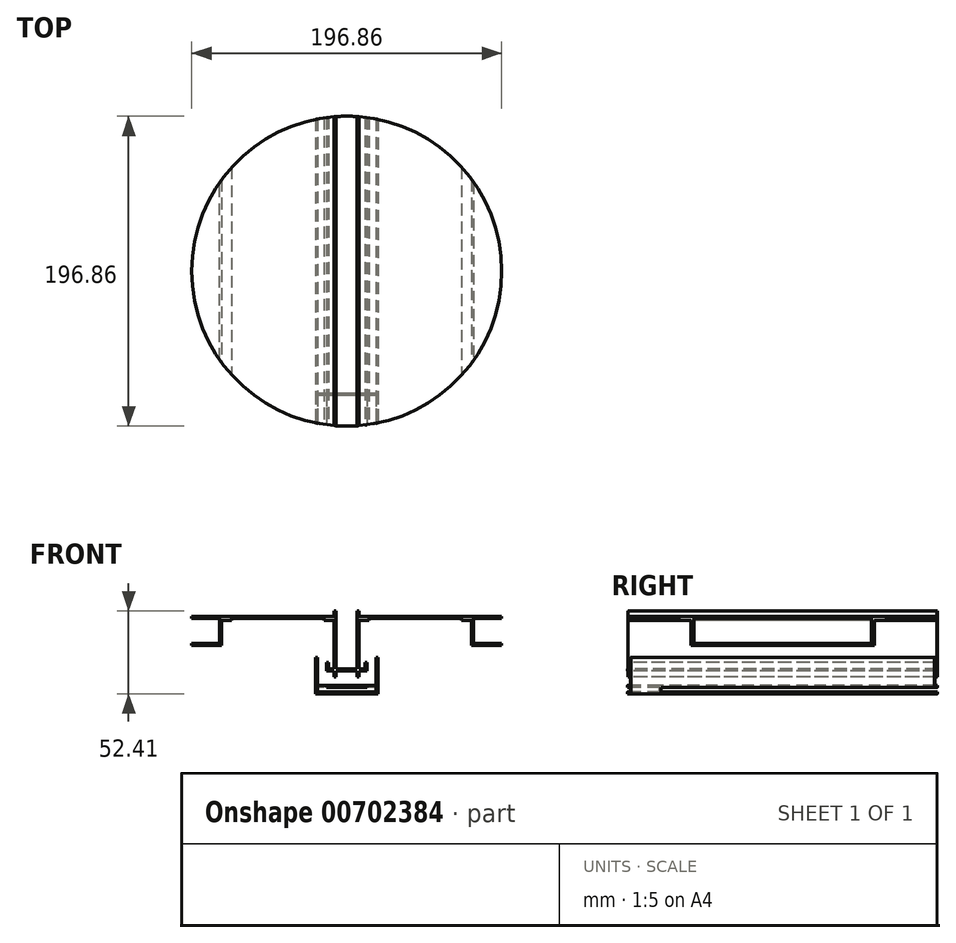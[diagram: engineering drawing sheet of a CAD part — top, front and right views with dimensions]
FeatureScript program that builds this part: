
annotation { "Feature Type Name" : "Feature", "Feature Type Description" : "" }
export const myFeature = defineFeature(function(context is Context, id is Id, definition is map)
    precondition{}
    {
        {
            var Q0;
            Q0=qCreatedBy(makeId("Top.planeOp"),FACE);
            var sketch = newSketch(context, id + "F0", { "sketchPlane" : qUnion([Q0])});
            skCircle(sketch, "E0", {"center": v(0, 0) * mm, "radius": 98.42 * mm});
            skLineSegment(sketch, "E1", {"start": v(0, 98.42) * mm, "end": v(0, -98.42) * mm, "construction": true});
            skLineSegment(sketch, "E2", {"start": v(-79.11, 58.56) * mm, "end": v(-79.11, -58.56) * mm, "construction": true});
            skLineSegment(sketch, "E3", {"start": v(79.11, 58.56) * mm, "end": v(79.11, -58.56) * mm, "construction": true});
            skLineSegment(sketch, "E4", {"start": v(0, 0) * mm, "end": v(79.11, 0) * mm, "construction": true});
            skLineSegment(sketch, "E5", {"start": v(79.11, 0) * mm, "end": v(98.42, 0) * mm, "construction": true});
            skLineSegment(sketch, "E6", {"start": v(0, 0) * mm, "end": v(-79.11, 0) * mm, "construction": true});
            skLineSegment(sketch, "E7", {"start": v(-79.11, 0) * mm, "end": v(-98.42, 0) * mm, "construction": true});
            skLineSegment(sketch, "E8", {"start": v(-7.94, 98.1) * mm, "end": v(-7.94, -98.1) * mm});
            skLineSegment(sketch, "E9", {"start": v(7.94, 98.1) * mm, "end": v(7.94, -98.1) * mm});
            skSolve(sketch);
        }
        {
            var Q0;
            {var subQ0=sQuery(id+"F0.wireOp",EDGE,"E8");Q0=makeQuery(id+"F0.imprint","IMPRINT",FACE,{"disambiguationData":[TD([[makeQuery(id+"F0.imprint","IMPRINT",EDGE,{"derivedFrom":subQ0}),-1.0]])]});}
            var Q1;
            {var subQ0=sQuery(id+"F0.wireOp",EDGE,"E9");Q1=makeQuery(id+"F0.imprint","IMPRINT",FACE,{"disambiguationData":[TD([[makeQuery(id+"F0.imprint","IMPRINT",EDGE,{"derivedFrom":subQ0}),1.0]])]});}
            extrude(context, id + "F1", {"entities" : qUnion([Q0, Q1]), "depth" : 1.27 * mm, "offsetDistance" : 25.4 * mm});
        }
        {
            var Q0;
            Q0=qCreatedBy(makeId("Top.planeOp"),FACE);
            var sketch = newSketch(context, id + "F2", { "sketchPlane" : qUnion([Q0])});
            skCircle(sketch, "E10", {"center": v(0, 0) * mm, "radius": 98.43 * mm, "construction": true});
            skLineSegment(sketch, "E11", {"start": v(0, 98.43) * mm, "end": v(0, -98.43) * mm, "construction": true});
            skLineSegment(sketch, "E12", {"start": v(-7.94, 98.1) * mm, "end": v(-7.94, -98.1) * mm});
            skLineSegment(sketch, "E13", {"start": v(7.94, 98.1) * mm, "end": v(7.94, -98.1) * mm});
            skLineSegment(sketch, "E14", {"start": v(-14.29, 97.38) * mm, "end": v(-14.29, -97.38) * mm});
            skLineSegment(sketch, "E15", {"start": v(14.29, 97.38) * mm, "end": v(14.29, -97.38) * mm});
            skLineSegment(sketch, "E16", {"start": v(-6.67, 98.2) * mm, "end": v(-6.67, -98.2) * mm});
            skLineSegment(sketch, "E17", {"start": v(6.67, -98.2) * mm, "end": v(6.67, 98.2) * mm});
            skArc(sketch, "E18", {"start": v(-14.29, 97.38) * mm, "mid": v(-11.12, 97.8) * mm, "end": v(-7.94, 98.1) * mm});
            skArc(sketch, "E19", {"start": v(-7.94, 98.1) * mm, "mid": v(-7.3, 98.15) * mm, "end": v(-6.67, 98.2) * mm});
            skArc(sketch, "E20", {"start": v(6.67, 98.2) * mm, "mid": v(7.3, 98.15) * mm, "end": v(7.94, 98.1) * mm});
            skArc(sketch, "E21", {"start": v(7.94, 98.1) * mm, "mid": v(11.12, 97.8) * mm, "end": v(14.29, 97.38) * mm});
            skArc(sketch, "E22", {"start": v(14.29, -97.38) * mm, "mid": v(11.12, -97.8) * mm, "end": v(7.94, -98.1) * mm});
            skArc(sketch, "E23", {"start": v(7.94, -98.1) * mm, "mid": v(7.3, -98.15) * mm, "end": v(6.67, -98.2) * mm});
            skArc(sketch, "E24", {"start": v(-6.67, -98.2) * mm, "mid": v(-7.3, -98.15) * mm, "end": v(-7.94, -98.1) * mm});
            skArc(sketch, "E25", {"start": v(-7.94, -98.1) * mm, "mid": v(-11.12, -97.8) * mm, "end": v(-14.29, -97.38) * mm});
            skSolve(sketch);
        }
        {
            var Q0;
            Q0=makeQuery(id+"F2.imprint","IMPRINT",FACE,{"disambiguationData":[TD([[makeQuery(id+"F2.imprint","IMPRINT",EDGE,{"derivedFrom":sQuery(id+"F2.wireOp",EDGE,"E12")}),-1.0]])]});
            var Q1;
            Q1=makeQuery(id+"F2.imprint","IMPRINT",FACE,{"disambiguationData":[TD([[makeQuery(id+"F2.imprint","IMPRINT",EDGE,{"derivedFrom":sQuery(id+"F2.wireOp",EDGE,"E13")}),1.0]])]});
            extrude(context, id + "F3", {"entities" : qUnion([Q0, Q1]), "oppositeDirection" : true, "depth" : 1.27 * mm, "offsetDistance" : 25.4 * mm});
        }
        {
            var Q0;
            Q0=makeQuery(id+"F2.imprint","IMPRINT",FACE,{"disambiguationData":[TD([[makeQuery(id+"F2.imprint","IMPRINT",EDGE,{"derivedFrom":sQuery(id+"F2.wireOp",EDGE,"E12")}),1.0]])]});
            var Q1;
            Q1=makeQuery(id+"F2.imprint","IMPRINT",FACE,{"disambiguationData":[TD([[makeQuery(id+"F2.imprint","IMPRINT",EDGE,{"derivedFrom":sQuery(id+"F2.wireOp",EDGE,"E13")}),-1.0]])]});
            extrude(context, id + "F4", {"entities" : qUnion([Q0, Q1]), "operationType" : NewBodyOperationType.ADD, "depth" : 4.5 * mm, "offsetDistance" : 25.4 * mm, "hasSecondDirection" : true, "secondDirectionOppositeDirection" : true, "secondDirectionDepth" : 29.3 * mm});
        }
        {
            var Q0;
            Q0=makeQuery(id+"F2.imprint","IMPRINT",FACE,{"disambiguationData":[TD([[makeQuery(id+"F2.imprint","IMPRINT",EDGE,{"derivedFrom":sQuery(id+"F2.wireOp",EDGE,"E12")}),-1.0]])]});
            var Q1;
            Q1=makeQuery(id+"F2.imprint","IMPRINT",FACE,{"disambiguationData":[TD([[makeQuery(id+"F2.imprint","IMPRINT",EDGE,{"derivedFrom":sQuery(id+"F2.wireOp",EDGE,"E13")}),1.0]])]});
            extrude(context, id + "F5", {"entities" : qUnion([Q0, Q1]), "oppositeDirection" : true, "depth" : 1.27 * mm, "offsetDistance" : 25.4 * mm});
        }
        {
            var Q0;
            Q0=makeQuery(id+"F2.imprint","IMPRINT",FACE,{"disambiguationData":[TD([[makeQuery(id+"F2.imprint","IMPRINT",EDGE,{"derivedFrom":sQuery(id+"F2.wireOp",EDGE,"E12")}),1.0]])]});
            var Q1;
            Q1=makeQuery(id+"F2.imprint","IMPRINT",FACE,{"disambiguationData":[TD([[makeQuery(id+"F2.imprint","IMPRINT",EDGE,{"derivedFrom":sQuery(id+"F2.wireOp",EDGE,"E13")}),-1.0]])]});
            extrude(context, id + "F6", {"entities" : qUnion([Q0, Q1]), "operationType" : NewBodyOperationType.ADD, "depth" : 3.45 * mm, "offsetDistance" : 25.4 * mm, "hasSecondDirection" : true, "secondDirectionOppositeDirection" : true, "secondDirectionDepth" : 30.63 * mm});
        }
        {
            var Q0;
            Q0=makeQuery(id+"F2.imprint","IMPRINT",FACE,{"disambiguationData":[TD([[makeQuery(id+"F2.imprint","IMPRINT",EDGE,{"derivedFrom":sQuery(id+"F2.wireOp",EDGE,"E12")}),-1.0]])]});
            var Q1;
            Q1=makeQuery(id+"F2.imprint","IMPRINT",FACE,{"disambiguationData":[TD([[makeQuery(id+"F2.imprint","IMPRINT",EDGE,{"derivedFrom":sQuery(id+"F2.wireOp",EDGE,"E13")}),1.0]])]});
            extrude(context, id + "F7", {"entities" : qUnion([Q0, Q1]), "oppositeDirection" : true, "depth" : 1.27 * mm, "offsetDistance" : 25.4 * mm});
        }
        {
            var Q0;
            Q0=makeQuery(id+"F2.imprint","IMPRINT",FACE,{"disambiguationData":[TD([[makeQuery(id+"F2.imprint","IMPRINT",EDGE,{"derivedFrom":sQuery(id+"F2.wireOp",EDGE,"E12")}),1.0]])]});
            var Q1;
            Q1=makeQuery(id+"F2.imprint","IMPRINT",FACE,{"disambiguationData":[TD([[makeQuery(id+"F2.imprint","IMPRINT",EDGE,{"derivedFrom":sQuery(id+"F2.wireOp",EDGE,"E13")}),-1.0]])]});
            extrude(context, id + "F8", {"entities" : qUnion([Q0, Q1]), "operationType" : NewBodyOperationType.ADD, "depth" : 3.45 * mm, "offsetDistance" : 25.4 * mm, "hasSecondDirection" : true, "secondDirectionOppositeDirection" : true, "secondDirectionDepth" : 36.98 * mm});
        }
        {
            var Q0;
            Q0=makeQuery(id+"F2.imprint","IMPRINT",FACE,{"disambiguationData":[TD([[makeQuery(id+"F2.imprint","IMPRINT",EDGE,{"derivedFrom":sQuery(id+"F2.wireOp",EDGE,"E12")}),-1.0]])]});
            var Q1;
            Q1=makeQuery(id+"F2.imprint","IMPRINT",FACE,{"disambiguationData":[TD([[makeQuery(id+"F2.imprint","IMPRINT",EDGE,{"derivedFrom":sQuery(id+"F2.wireOp",EDGE,"E13")}),1.0]])]});
            extrude(context, id + "F9", {"entities" : qUnion([Q0, Q1]), "oppositeDirection" : true, "depth" : 1.27 * mm, "offsetDistance" : 25.4 * mm});
        }
        {
            var Q0;
            Q0=makeQuery(id+"F2.imprint","IMPRINT",FACE,{"disambiguationData":[TD([[makeQuery(id+"F2.imprint","IMPRINT",EDGE,{"derivedFrom":sQuery(id+"F2.wireOp",EDGE,"E12")}),1.0]])]});
            var Q1;
            Q1=makeQuery(id+"F2.imprint","IMPRINT",FACE,{"disambiguationData":[TD([[makeQuery(id+"F2.imprint","IMPRINT",EDGE,{"derivedFrom":sQuery(id+"F2.wireOp",EDGE,"E13")}),-1.0]])]});
            extrude(context, id + "F10", {"entities" : qUnion([Q0, Q1]), "operationType" : NewBodyOperationType.ADD, "depth" : 3.45 * mm, "offsetDistance" : 25.4 * mm, "hasSecondDirection" : true, "secondDirectionOppositeDirection" : true, "secondDirectionDepth" : 37.24 * mm});
        }
        {
            var Q0;
            Q0=makeQuery(id+"F2.imprint","IMPRINT",FACE,{"disambiguationData":[TD([[makeQuery(id+"F2.imprint","IMPRINT",EDGE,{"derivedFrom":sQuery(id+"F2.wireOp",EDGE,"E12")}),-1.0]])]});
            var Q1;
            Q1=makeQuery(id+"F2.imprint","IMPRINT",FACE,{"disambiguationData":[TD([[makeQuery(id+"F2.imprint","IMPRINT",EDGE,{"derivedFrom":sQuery(id+"F2.wireOp",EDGE,"E13")}),1.0]])]});
            extrude(context, id + "F11", {"entities" : qUnion([Q0, Q1]), "oppositeDirection" : true, "depth" : 1.27 * mm, "offsetDistance" : 25.4 * mm});
        }
        {
            var Q0;
            Q0=makeQuery(id+"F2.imprint","IMPRINT",FACE,{"disambiguationData":[TD([[makeQuery(id+"F2.imprint","IMPRINT",EDGE,{"derivedFrom":sQuery(id+"F2.wireOp",EDGE,"E12")}),1.0]])]});
            var Q1;
            Q1=makeQuery(id+"F2.imprint","IMPRINT",FACE,{"disambiguationData":[TD([[makeQuery(id+"F2.imprint","IMPRINT",EDGE,{"derivedFrom":sQuery(id+"F2.wireOp",EDGE,"E13")}),-1.0]])]});
            extrude(context, id + "F12", {"entities" : qUnion([Q0, Q1]), "operationType" : NewBodyOperationType.ADD, "depth" : 3.45 * mm, "offsetDistance" : 25.4 * mm, "hasSecondDirection" : true, "secondDirectionOppositeDirection" : true, "secondDirectionDepth" : 30.9 * mm});
        }
        {
            var Q0;
            Q0=qCreatedBy(makeId("Top.planeOp"),FACE);
            var sketch = newSketch(context, id + "F13", { "sketchPlane" : qUnion([Q0])});
            skCircle(sketch, "E26", {"center": v(0, 0) * mm, "radius": 98.43 * mm, "construction": true});
            skLineSegment(sketch, "E27", {"start": v(-98.43, 0) * mm, "end": v(98.43, 0) * mm, "construction": true});
            skLineSegment(sketch, "E28", {"start": v(0, 98.43) * mm, "end": v(0, -98.43) * mm, "construction": true});
            skLineSegment(sketch, "E29", {"start": v(-7.94, 98.1) * mm, "end": v(-7.94, -98.1) * mm});
            skLineSegment(sketch, "E30", {"start": v(7.94, 98.1) * mm, "end": v(7.94, -98.1) * mm});
            skLineSegment(sketch, "E31", {"start": v(79.38, 58.2) * mm, "end": v(79.38, -58.2) * mm});
            skLineSegment(sketch, "E32", {"start": v(-79.38, 58.2) * mm, "end": v(-79.38, -58.2) * mm});
            skLineSegment(sketch, "E33", {"start": v(-14.29, 97.38) * mm, "end": v(-14.29, -97.38) * mm});
            skLineSegment(sketch, "E34", {"start": v(14.29, 97.38) * mm, "end": v(14.29, -97.38) * mm});
            skLineSegment(sketch, "E35", {"start": v(-6.67, 98.2) * mm, "end": v(-6.67, -98.2) * mm});
            skLineSegment(sketch, "E36", {"start": v(6.67, 98.2) * mm, "end": v(6.67, -98.2) * mm});
            skLineSegment(sketch, "E37", {"start": v(-73.03, 66) * mm, "end": v(-73.03, -66) * mm});
            skLineSegment(sketch, "E38", {"start": v(-80.65, 56.43) * mm, "end": v(-80.65, -56.43) * mm});
            skLineSegment(sketch, "E39", {"start": v(73.03, 66) * mm, "end": v(73.03, -66) * mm});
            skLineSegment(sketch, "E40", {"start": v(80.65, 56.43) * mm, "end": v(80.65, -56.43) * mm});
            skArc(sketch, "E41", {"start": v(-6.67, -98.2) * mm, "mid": v(-98.43, 0) * mm, "end": v(-6.67, 98.2) * mm});
            skArc(sketch, "E42", {"start": v(6.67, -98.2) * mm, "mid": v(98.43, 0) * mm, "end": v(6.67, 98.2) * mm});
            skSolve(sketch);
        }
        {
            var Q0;
            {var subQ0=sQuery(id+"F13.wireOp",EDGE,"E32");Q0=makeQuery(id+"F13.imprint","IMPRINT",FACE,{"disambiguationData":[TD([[makeQuery(id+"F13.imprint","IMPRINT",EDGE,{"derivedFrom":subQ0}),1.0]])]});}
            var Q1;
            {var subQ0=sQuery(id+"F13.wireOp",EDGE,"E33");Q1=makeQuery(id+"F13.imprint","IMPRINT",FACE,{"disambiguationData":[TD([[makeQuery(id+"F13.imprint","IMPRINT",EDGE,{"derivedFrom":subQ0}),-1.0]])]});}
            var Q2;
            {var subQ0=sQuery(id+"F13.wireOp",EDGE,"E29");Q2=makeQuery(id+"F13.imprint","IMPRINT",FACE,{"disambiguationData":[TD([[makeQuery(id+"F13.imprint","IMPRINT",EDGE,{"derivedFrom":subQ0}),-1.0]])]});}
            var Q3;
            {var subQ0=sQuery(id+"F13.wireOp",EDGE,"E30");Q3=makeQuery(id+"F13.imprint","IMPRINT",FACE,{"disambiguationData":[TD([[makeQuery(id+"F13.imprint","IMPRINT",EDGE,{"derivedFrom":subQ0}),1.0]])]});}
            var Q4;
            {var subQ0=sQuery(id+"F13.wireOp",EDGE,"E34");Q4=makeQuery(id+"F13.imprint","IMPRINT",FACE,{"disambiguationData":[TD([[makeQuery(id+"F13.imprint","IMPRINT",EDGE,{"derivedFrom":subQ0}),1.0]])]});}
            var Q5;
            {var subQ0=sQuery(id+"F13.wireOp",EDGE,"E31");Q5=makeQuery(id+"F13.imprint","IMPRINT",FACE,{"disambiguationData":[TD([[makeQuery(id+"F13.imprint","IMPRINT",EDGE,{"derivedFrom":subQ0}),-1.0]])]});}
            extrude(context, id + "F14", {"entities" : qUnion([Q0, Q1, Q2, Q3, Q4, Q5]), "depth" : 1.27 * mm, "offsetDistance" : 25.4 * mm});
        }
        {
            var Q0;
            {var subQ0=sQuery(id+"F13.wireOp",EDGE,"E29");Q0=makeQuery(id+"F13.imprint","IMPRINT",FACE,{"disambiguationData":[TD([[makeQuery(id+"F13.imprint","IMPRINT",EDGE,{"derivedFrom":subQ0}),-1.0]])]});}
            var Q1;
            {var subQ0=sQuery(id+"F13.wireOp",EDGE,"E30");Q1=makeQuery(id+"F13.imprint","IMPRINT",FACE,{"disambiguationData":[TD([[makeQuery(id+"F13.imprint","IMPRINT",EDGE,{"derivedFrom":subQ0}),1.0]])]});}
            extrude(context, id + "F15", {"entities" : qUnion([Q0, Q1]), "oppositeDirection" : true, "depth" : 1.27 * mm, "offsetDistance" : 25.4 * mm});
        }
        {
            var Q0;
            {var subQ0=sQuery(id+"F13.wireOp",EDGE,"E29");Q0=makeQuery(id+"F13.imprint","IMPRINT",FACE,{"disambiguationData":[TD([[makeQuery(id+"F13.imprint","IMPRINT",EDGE,{"derivedFrom":subQ0}),1.0]])]});}
            var Q1;
            {var subQ0=sQuery(id+"F13.wireOp",EDGE,"E30");Q1=makeQuery(id+"F13.imprint","IMPRINT",FACE,{"disambiguationData":[TD([[makeQuery(id+"F13.imprint","IMPRINT",EDGE,{"derivedFrom":subQ0}),-1.0]])]});}
            extrude(context, id + "F16", {"entities" : qUnion([Q0, Q1]), "operationType" : NewBodyOperationType.ADD, "depth" : 3.45 * mm, "offsetDistance" : 25.4 * mm, "hasSecondDirection" : true, "secondDirectionOppositeDirection" : true, "secondDirectionDepth" : 30.63 * mm});
        }
        {
            var Q0;
            {var subQ0=sQuery(id+"F13.wireOp",EDGE,"E32");Q0=makeQuery(id+"F13.imprint","IMPRINT",FACE,{"disambiguationData":[TD([[makeQuery(id+"F13.imprint","IMPRINT",EDGE,{"derivedFrom":subQ0}),1.0]])]});}
            var Q1;
            {var subQ0=sQuery(id+"F13.wireOp",EDGE,"E31");Q1=makeQuery(id+"F13.imprint","IMPRINT",FACE,{"disambiguationData":[TD([[makeQuery(id+"F13.imprint","IMPRINT",EDGE,{"derivedFrom":subQ0}),-1.0]])]});}
            extrude(context, id + "F17", {"entities" : qUnion([Q0, Q1]), "oppositeDirection" : true, "depth" : 1.27 * mm, "offsetDistance" : 25.4 * mm});
        }
        {
            var Q0;
            {var subQ0=sQuery(id+"F13.wireOp",EDGE,"E32");Q0=makeQuery(id+"F13.imprint","IMPRINT",FACE,{"disambiguationData":[TD([[makeQuery(id+"F13.imprint","IMPRINT",EDGE,{"derivedFrom":subQ0}),-1.0]])]});}
            var Q1;
            {var subQ0=sQuery(id+"F13.wireOp",EDGE,"E31");Q1=makeQuery(id+"F13.imprint","IMPRINT",FACE,{"disambiguationData":[TD([[makeQuery(id+"F13.imprint","IMPRINT",EDGE,{"derivedFrom":subQ0}),1.0]])]});}
            extrude(context, id + "F18", {"entities" : qUnion([Q0, Q1]), "operationType" : NewBodyOperationType.ADD, "depth" : 1.27 * mm, "offsetDistance" : 25.4 * mm, "hasSecondDirection" : true, "secondDirectionOppositeDirection" : true, "secondDirectionDepth" : 15.88 * mm});
        }
        {
            var Q0;
            {var subQ0=sQuery(id+"F13.wireOp",EDGE,"E38");Q0=makeQuery(id+"F13.imprint","IMPRINT",FACE,{"disambiguationData":[TD([[makeQuery(id+"F13.imprint","IMPRINT",EDGE,{"derivedFrom":subQ0}),-1.0]])]});}
            var Q1;
            {var subQ0=sQuery(id+"F13.wireOp",EDGE,"E32");Q1=makeQuery(id+"F13.imprint","IMPRINT",FACE,{"disambiguationData":[TD([[makeQuery(id+"F13.imprint","IMPRINT",EDGE,{"derivedFrom":subQ0}),-1.0]])]});}
            var Q2;
            {var subQ0=sQuery(id+"F13.wireOp",EDGE,"E40");Q2=makeQuery(id+"F13.imprint","IMPRINT",FACE,{"disambiguationData":[TD([[makeQuery(id+"F13.imprint","IMPRINT",EDGE,{"derivedFrom":subQ0}),1.0]])]});}
            var Q3;
            {var subQ0=sQuery(id+"F13.wireOp",EDGE,"E31");Q3=makeQuery(id+"F13.imprint","IMPRINT",FACE,{"disambiguationData":[TD([[makeQuery(id+"F13.imprint","IMPRINT",EDGE,{"derivedFrom":subQ0}),1.0]])]});}
            extrude(context, id + "F19", {"entities" : qUnion([Q0, Q1, Q2, Q3]), "oppositeDirection" : true, "depth" : 17.14 * mm, "offsetDistance" : 25.4 * mm, "hasSecondDirection" : true, "secondDirectionOppositeDirection" : true, "secondDirectionDepth" : 15.88 * mm});
        }
        {
            var Q0;
            Q0=qCreatedBy(makeId("Top.planeOp"),FACE);
            var sketch = newSketch(context, id + "F20", { "sketchPlane" : qUnion([Q0])});
            skCircle(sketch, "E43", {"center": v(0, 0) * mm, "radius": 98.43 * mm, "construction": true});
            skLineSegment(sketch, "E44", {"start": v(-98.43, 0) * mm, "end": v(98.43, 0) * mm, "construction": true});
            skLineSegment(sketch, "E45", {"start": v(0, 98.43) * mm, "end": v(0, -98.43) * mm, "construction": true});
            skLineSegment(sketch, "E46", {"start": v(-7.94, 98.1) * mm, "end": v(-7.94, -98.1) * mm});
            skLineSegment(sketch, "E47", {"start": v(7.94, 98.1) * mm, "end": v(7.94, -98.1) * mm});
            skLineSegment(sketch, "E48", {"start": v(-14.29, 97.38) * mm, "end": v(-14.29, -97.38) * mm});
            skLineSegment(sketch, "E49", {"start": v(14.29, 97.38) * mm, "end": v(14.29, -97.38) * mm});
            skLineSegment(sketch, "E50", {"start": v(-6.67, 98.2) * mm, "end": v(-6.67, -98.2) * mm});
            skLineSegment(sketch, "E51", {"start": v(6.67, 98.2) * mm, "end": v(6.67, -98.2) * mm});
            skArc(sketch, "E52", {"start": v(-14.29, 97.38) * mm, "mid": v(-10.49, 97.86) * mm, "end": v(-6.67, 98.2) * mm});
            skArc(sketch, "E53", {"start": v(6.67, 98.2) * mm, "mid": v(10.49, 97.86) * mm, "end": v(14.29, 97.38) * mm});
            skArc(sketch, "E54", {"start": v(14.29, -97.38) * mm, "mid": v(10.49, -97.86) * mm, "end": v(6.67, -98.2) * mm});
            skArc(sketch, "E55", {"start": v(-6.67, -98.2) * mm, "mid": v(-10.49, -97.86) * mm, "end": v(-14.29, -97.38) * mm});
            skSolve(sketch);
        }
        {
            var Q0;
            {var subQ0=sQuery(id+"F20.wireOp",EDGE,"E46");Q0=makeQuery(id+"F20.imprint","IMPRINT",FACE,{"disambiguationData":[TD([[makeQuery(id+"F20.imprint","IMPRINT",EDGE,{"derivedFrom":subQ0}),-1.0]])]});}
            var Q1;
            {var subQ0=sQuery(id+"F20.wireOp",EDGE,"E47");Q1=makeQuery(id+"F20.imprint","IMPRINT",FACE,{"disambiguationData":[TD([[makeQuery(id+"F20.imprint","IMPRINT",EDGE,{"derivedFrom":subQ0}),1.0]])]});}
            extrude(context, id + "F21", {"entities" : qUnion([Q0, Q1]), "oppositeDirection" : true, "depth" : 1.27 * mm, "offsetDistance" : 25.4 * mm});
        }
        {
            var Q0;
            {var subQ0=sQuery(id+"F20.wireOp",EDGE,"E46");Q0=makeQuery(id+"F20.imprint","IMPRINT",FACE,{"disambiguationData":[TD([[makeQuery(id+"F20.imprint","IMPRINT",EDGE,{"derivedFrom":subQ0}),1.0]])]});}
            var Q1;
            {var subQ0=sQuery(id+"F20.wireOp",EDGE,"E47");Q1=makeQuery(id+"F20.imprint","IMPRINT",FACE,{"disambiguationData":[TD([[makeQuery(id+"F20.imprint","IMPRINT",EDGE,{"derivedFrom":subQ0}),-1.0]])]});}
            extrude(context, id + "F22", {"entities" : qUnion([Q0, Q1]), "operationType" : NewBodyOperationType.ADD, "depth" : 3.45 * mm, "offsetDistance" : 25.4 * mm, "hasSecondDirection" : true, "secondDirectionOppositeDirection" : true, "secondDirectionDepth" : 30.16 * mm});
        }
        {
            var Q0;
            Q0=qCreatedBy(makeId("Top.planeOp"),FACE);
            var sketch = newSketch(context, id + "F23", { "sketchPlane" : qUnion([Q0])});
            skCircle(sketch, "E56", {"center": v(0, 0) * mm, "radius": 98.43 * mm, "construction": true});
            skLineSegment(sketch, "E57", {"start": v(-98.43, 0) * mm, "end": v(98.43, 0) * mm, "construction": true});
            skLineSegment(sketch, "E58", {"start": v(0, 98.43) * mm, "end": v(0, -98.43) * mm, "construction": true});
            skLineSegment(sketch, "E59", {"start": v(-11.64, 97.73) * mm, "end": v(-11.64, -97.73) * mm});
            skLineSegment(sketch, "E60", {"start": v(11.64, 97.73) * mm, "end": v(11.64, -97.73) * mm});
            skLineSegment(sketch, "E61", {"start": v(-12.91, 97.57) * mm, "end": v(-12.91, -97.57) * mm});
            skLineSegment(sketch, "E62", {"start": v(12.91, 97.57) * mm, "end": v(12.91, -97.57) * mm});
            skArc(sketch, "E63", {"start": v(-12.91, 97.57) * mm, "mid": v(0, 98.43) * mm, "end": v(12.91, 97.57) * mm});
            skArc(sketch, "E64", {"start": v(12.91, -97.57) * mm, "mid": v(0, -98.43) * mm, "end": v(-12.91, -97.57) * mm});
            skLineSegment(sketch, "E65", {"start": v(-18.65, 96.64) * mm, "end": v(-18.65, -96.64) * mm});
            skLineSegment(sketch, "E66", {"start": v(18.65, 96.64) * mm, "end": v(18.65, -96.64) * mm});
            skLineSegment(sketch, "E67", {"start": v(-19.92, 96.39) * mm, "end": v(-19.92, -96.39) * mm});
            skLineSegment(sketch, "E68", {"start": v(19.92, 96.39) * mm, "end": v(19.92, -96.39) * mm});
            skArc(sketch, "E69", {"start": v(19.92, -96.39) * mm, "mid": v(0, -98.43) * mm, "end": v(-19.92, -96.39) * mm});
            skArc(sketch, "E70", {"start": v(-19.92, 96.39) * mm, "mid": v(0, 98.43) * mm, "end": v(19.92, 96.39) * mm});
            skLineSegment(sketch, "E71", {"start": v(-19.92, -78.52) * mm, "end": v(19.92, -78.52) * mm});
            skLineSegment(sketch, "E72", {"start": v(-19.92, -77.25) * mm, "end": v(19.92, -77.25) * mm});
            skSolve(sketch);
        }
        {
            var Q0;
            {var subQ0=sQuery(id+"F23.wireOp",EDGE,"E59");Q0=makeQuery(id+"F23.imprint","IMPRINT",FACE,{"disambiguationData":[TD([[makeQuery(id+"F23.imprint","IMPRINT",EDGE,{"derivedFrom":subQ0}),-1.0]])]});}
            var Q1;
            {var subQ0=sQuery(id+"F23.wireOp",EDGE,"E60");Q1=makeQuery(id+"F23.imprint","IMPRINT",FACE,{"disambiguationData":[TD([[makeQuery(id+"F23.imprint","IMPRINT",EDGE,{"derivedFrom":subQ0}),1.0]])]});}
            extrude(context, id + "F24", {"entities" : qUnion([Q0, Q1]), "oppositeDirection" : true, "depth" : 32.08 * mm, "offsetDistance" : 25.4 * mm, "hasSecondDirection" : true, "secondDirectionOppositeDirection" : true, "secondDirectionDepth" : 28.05 * mm});
        }
        {
            var Q0;
            {var subQ0=sQuery(id+"F23.wireOp",EDGE,"E59");Q0=makeQuery(id+"F23.imprint","IMPRINT",FACE,{"disambiguationData":[TD([[makeQuery(id+"F23.imprint","IMPRINT",EDGE,{"derivedFrom":subQ0}),1.0]])]});}
            var Q1;
            {var subQ0=sQuery(id+"F23.wireOp",EDGE,"E59");Q1=makeQuery(id+"F23.imprint","IMPRINT",FACE,{"disambiguationData":[TD([[makeQuery(id+"F23.imprint","IMPRINT",EDGE,{"derivedFrom":subQ0}),-1.0]])]});}
            var Q2;
            {var subQ0=sQuery(id+"F23.wireOp",EDGE,"E60");Q2=makeQuery(id+"F23.imprint","IMPRINT",FACE,{"disambiguationData":[TD([[makeQuery(id+"F23.imprint","IMPRINT",EDGE,{"derivedFrom":subQ0}),1.0]])]});}
            extrude(context, id + "F25", {"entities" : qUnion([Q0, Q1, Q2]), "operationType" : NewBodyOperationType.ADD, "oppositeDirection" : true, "depth" : 33.35 * mm, "offsetDistance" : 25.4 * mm, "hasSecondDirection" : true, "secondDirectionOppositeDirection" : true, "secondDirectionDepth" : 32.08 * mm});
        }
        {
            var Q0;
            {var subQ0=sQuery(id+"F23.wireOp",EDGE,"E70");var subQ1=sQuery(id+"F23.wireOp",EDGE,"E66");var subQ2=makeQuery(id+"F23.imprint","INTERSECT",VERTEX,{"derivedFrom":[subQ1,subQ0]});Q0=makeQuery(id+"F23.imprint","IMPRINT",FACE,{"disambiguationData":[TD([[makeQuery(id+"F23.imprint","IMPRINT",EDGE,{"disambiguationData":[TD([[subQ2,-1.0]])],"derivedFrom":subQ1}),1.0]])]});}
            var Q1;
            {var subQ0=sQuery(id+"F23.wireOp",EDGE,"E70");var subQ1=sQuery(id+"F23.wireOp",EDGE,"E65");var subQ2=makeQuery(id+"F23.imprint","INTERSECT",VERTEX,{"derivedFrom":[subQ1,subQ0]});Q1=makeQuery(id+"F23.imprint","IMPRINT",FACE,{"disambiguationData":[TD([[makeQuery(id+"F23.imprint","IMPRINT",EDGE,{"disambiguationData":[TD([[subQ2,-1.0]])],"derivedFrom":subQ1}),-1.0]])]});}
            extrude(context, id + "F26", {"entities" : qUnion([Q0, Q1]), "oppositeDirection" : true, "depth" : 42.53 * mm, "offsetDistance" : 25.4 * mm, "hasSecondDirection" : true, "secondDirectionOppositeDirection" : true, "secondDirectionDepth" : 24.94 * mm});
        }
        {
            var Q0;
            {var subQ0=sQuery(id+"F23.wireOp",EDGE,"E70");var subQ1=sQuery(id+"F23.wireOp",EDGE,"E59");var subQ2=makeQuery(id+"F23.imprint","INTERSECT",VERTEX,{"derivedFrom":[subQ1,subQ0]});Q0=makeQuery(id+"F23.imprint","IMPRINT",FACE,{"disambiguationData":[TD([[makeQuery(id+"F23.imprint","IMPRINT",EDGE,{"disambiguationData":[TD([[subQ2,-1.0]])],"derivedFrom":subQ1}),1.0]])]});}
            var Q1;
            {var subQ0=sQuery(id+"F23.wireOp",EDGE,"E72");var subQ1=sQuery(id+"F23.wireOp",EDGE,"E59");var subQ2=makeQuery(id+"F23.imprint","INTERSECT",VERTEX,{"derivedFrom":[subQ1,subQ0]});Q1=makeQuery(id+"F23.imprint","IMPRINT",FACE,{"disambiguationData":[TD([[makeQuery(id+"F23.imprint","IMPRINT",EDGE,{"disambiguationData":[TD([[subQ2,-1.0]])],"derivedFrom":subQ1}),1.0]])]});}
            var Q2;
            {var subQ0=sQuery(id+"F23.wireOp",EDGE,"E70");var subQ1=sQuery(id+"F23.wireOp",EDGE,"E65");var subQ2=makeQuery(id+"F23.imprint","INTERSECT",VERTEX,{"derivedFrom":[subQ1,subQ0]});Q2=makeQuery(id+"F23.imprint","IMPRINT",FACE,{"disambiguationData":[TD([[makeQuery(id+"F23.imprint","IMPRINT",EDGE,{"disambiguationData":[TD([[subQ2,-1.0]])],"derivedFrom":subQ1}),-1.0]])]});}
            var Q3;
            {var subQ0=sQuery(id+"F23.wireOp",EDGE,"E72");var subQ1=sQuery(id+"F23.wireOp",EDGE,"E65");var subQ2=makeQuery(id+"F23.imprint","INTERSECT",VERTEX,{"derivedFrom":[subQ1,subQ0]});Q3=makeQuery(id+"F23.imprint","IMPRINT",FACE,{"disambiguationData":[TD([[makeQuery(id+"F23.imprint","IMPRINT",EDGE,{"disambiguationData":[TD([[subQ2,-1.0]])],"derivedFrom":subQ1}),-1.0]])]});}
            var Q4;
            {var subQ0=sQuery(id+"F23.wireOp",EDGE,"E70");var subQ1=sQuery(id+"F23.wireOp",EDGE,"E61");var subQ2=makeQuery(id+"F23.imprint","INTERSECT",VERTEX,{"derivedFrom":[subQ1,subQ0]});Q4=makeQuery(id+"F23.imprint","IMPRINT",FACE,{"disambiguationData":[TD([[makeQuery(id+"F23.imprint","IMPRINT",EDGE,{"disambiguationData":[TD([[subQ2,-1.0]])],"derivedFrom":subQ1}),-1.0]])]});}
            var Q5;
            {var subQ0=sQuery(id+"F23.wireOp",EDGE,"E72");var subQ1=sQuery(id+"F23.wireOp",EDGE,"E61");var subQ2=makeQuery(id+"F23.imprint","INTERSECT",VERTEX,{"derivedFrom":[subQ1,subQ0]});Q5=makeQuery(id+"F23.imprint","IMPRINT",FACE,{"disambiguationData":[TD([[makeQuery(id+"F23.imprint","IMPRINT",EDGE,{"disambiguationData":[TD([[subQ2,-1.0]])],"derivedFrom":subQ1}),-1.0]])]});}
            var Q6;
            {var subQ0=sQuery(id+"F23.wireOp",EDGE,"E70");var subQ1=sQuery(id+"F23.wireOp",EDGE,"E59");var subQ2=makeQuery(id+"F23.imprint","INTERSECT",VERTEX,{"derivedFrom":[subQ1,subQ0]});Q6=makeQuery(id+"F23.imprint","IMPRINT",FACE,{"disambiguationData":[TD([[makeQuery(id+"F23.imprint","IMPRINT",EDGE,{"disambiguationData":[TD([[subQ2,-1.0]])],"derivedFrom":subQ1}),-1.0]])]});}
            var Q7;
            {var subQ0=sQuery(id+"F23.wireOp",EDGE,"E72");var subQ1=sQuery(id+"F23.wireOp",EDGE,"E59");var subQ2=makeQuery(id+"F23.imprint","INTERSECT",VERTEX,{"derivedFrom":[subQ1,subQ0]});Q7=makeQuery(id+"F23.imprint","IMPRINT",FACE,{"disambiguationData":[TD([[makeQuery(id+"F23.imprint","IMPRINT",EDGE,{"disambiguationData":[TD([[subQ2,-1.0]])],"derivedFrom":subQ1}),-1.0]])]});}
            var Q8;
            {var subQ0=sQuery(id+"F23.wireOp",EDGE,"E70");var subQ1=sQuery(id+"F23.wireOp",EDGE,"E60");var subQ2=makeQuery(id+"F23.imprint","INTERSECT",VERTEX,{"derivedFrom":[subQ1,subQ0]});Q8=makeQuery(id+"F23.imprint","IMPRINT",FACE,{"disambiguationData":[TD([[makeQuery(id+"F23.imprint","IMPRINT",EDGE,{"disambiguationData":[TD([[subQ2,-1.0]])],"derivedFrom":subQ1}),1.0]])]});}
            var Q9;
            {var subQ0=sQuery(id+"F23.wireOp",EDGE,"E72");var subQ1=sQuery(id+"F23.wireOp",EDGE,"E60");var subQ2=makeQuery(id+"F23.imprint","INTERSECT",VERTEX,{"derivedFrom":[subQ1,subQ0]});Q9=makeQuery(id+"F23.imprint","IMPRINT",FACE,{"disambiguationData":[TD([[makeQuery(id+"F23.imprint","IMPRINT",EDGE,{"disambiguationData":[TD([[subQ2,-1.0]])],"derivedFrom":subQ1}),1.0]])]});}
            var Q10;
            {var subQ0=sQuery(id+"F23.wireOp",EDGE,"E70");var subQ1=sQuery(id+"F23.wireOp",EDGE,"E62");var subQ2=makeQuery(id+"F23.imprint","INTERSECT",VERTEX,{"derivedFrom":[subQ1,subQ0]});Q10=makeQuery(id+"F23.imprint","IMPRINT",FACE,{"disambiguationData":[TD([[makeQuery(id+"F23.imprint","IMPRINT",EDGE,{"disambiguationData":[TD([[subQ2,-1.0]])],"derivedFrom":subQ1}),1.0]])]});}
            var Q11;
            {var subQ0=sQuery(id+"F23.wireOp",EDGE,"E72");var subQ1=sQuery(id+"F23.wireOp",EDGE,"E62");var subQ2=makeQuery(id+"F23.imprint","INTERSECT",VERTEX,{"derivedFrom":[subQ1,subQ0]});Q11=makeQuery(id+"F23.imprint","IMPRINT",FACE,{"disambiguationData":[TD([[makeQuery(id+"F23.imprint","IMPRINT",EDGE,{"disambiguationData":[TD([[subQ2,-1.0]])],"derivedFrom":subQ1}),1.0]])]});}
            var Q12;
            {var subQ0=sQuery(id+"F23.wireOp",EDGE,"E70");var subQ1=sQuery(id+"F23.wireOp",EDGE,"E66");var subQ2=makeQuery(id+"F23.imprint","INTERSECT",VERTEX,{"derivedFrom":[subQ1,subQ0]});Q12=makeQuery(id+"F23.imprint","IMPRINT",FACE,{"disambiguationData":[TD([[makeQuery(id+"F23.imprint","IMPRINT",EDGE,{"disambiguationData":[TD([[subQ2,-1.0]])],"derivedFrom":subQ1}),1.0]])]});}
            var Q13;
            {var subQ0=sQuery(id+"F23.wireOp",EDGE,"E72");var subQ1=sQuery(id+"F23.wireOp",EDGE,"E66");var subQ2=makeQuery(id+"F23.imprint","INTERSECT",VERTEX,{"derivedFrom":[subQ1,subQ0]});Q13=makeQuery(id+"F23.imprint","IMPRINT",FACE,{"disambiguationData":[TD([[makeQuery(id+"F23.imprint","IMPRINT",EDGE,{"disambiguationData":[TD([[subQ2,-1.0]])],"derivedFrom":subQ1}),1.0]])]});}
            extrude(context, id + "F27", {"entities" : qUnion([Q0, Q1, Q2, Q3, Q4, Q5, Q6, Q7, Q8, Q9, Q10, Q11, Q12, Q13]), "operationType" : NewBodyOperationType.ADD, "oppositeDirection" : true, "depth" : 43.8 * mm, "offsetDistance" : 25.4 * mm, "hasSecondDirection" : true, "secondDirectionOppositeDirection" : true, "secondDirectionDepth" : 42.53 * mm});
        }
        {
            var Q0;
            {var subQ0=sQuery(id+"F23.wireOp",EDGE,"E69");var subQ1=sQuery(id+"F23.wireOp",EDGE,"E65");var subQ2=makeQuery(id+"F23.imprint","INTERSECT",VERTEX,{"derivedFrom":[subQ1,subQ0]});Q0=makeQuery(id+"F23.imprint","IMPRINT",FACE,{"disambiguationData":[TD([[makeQuery(id+"F23.imprint","IMPRINT",EDGE,{"disambiguationData":[TD([[subQ2,1.0]])],"derivedFrom":subQ1}),-1.0]])]});}
            var Q1;
            {var subQ0=sQuery(id+"F23.wireOp",EDGE,"E72");var subQ1=sQuery(id+"F23.wireOp",EDGE,"E65");var subQ2=makeQuery(id+"F23.imprint","INTERSECT",VERTEX,{"derivedFrom":[subQ1,subQ0]});Q1=makeQuery(id+"F23.imprint","IMPRINT",FACE,{"disambiguationData":[TD([[makeQuery(id+"F23.imprint","IMPRINT",EDGE,{"disambiguationData":[TD([[subQ2,-1.0]])],"derivedFrom":subQ1}),-1.0]])]});}
            var Q2;
            {var subQ0=sQuery(id+"F23.wireOp",EDGE,"E72");var subQ1=sQuery(id+"F23.wireOp",EDGE,"E66");var subQ2=makeQuery(id+"F23.imprint","INTERSECT",VERTEX,{"derivedFrom":[subQ1,subQ0]});Q2=makeQuery(id+"F23.imprint","IMPRINT",FACE,{"disambiguationData":[TD([[makeQuery(id+"F23.imprint","IMPRINT",EDGE,{"disambiguationData":[TD([[subQ2,-1.0]])],"derivedFrom":subQ1}),1.0]])]});}
            var Q3;
            {var subQ0=sQuery(id+"F23.wireOp",EDGE,"E69");var subQ1=sQuery(id+"F23.wireOp",EDGE,"E66");var subQ2=makeQuery(id+"F23.imprint","INTERSECT",VERTEX,{"derivedFrom":[subQ1,subQ0]});Q3=makeQuery(id+"F23.imprint","IMPRINT",FACE,{"disambiguationData":[TD([[makeQuery(id+"F23.imprint","IMPRINT",EDGE,{"disambiguationData":[TD([[subQ2,1.0]])],"derivedFrom":subQ1}),1.0]])]});}
            extrude(context, id + "F28", {"entities" : qUnion([Q0, Q1, Q2, Q3]), "operationType" : NewBodyOperationType.ADD, "oppositeDirection" : true, "depth" : 46.63 * mm, "offsetDistance" : 25.4 * mm, "hasSecondDirection" : true, "secondDirectionOppositeDirection" : true, "secondDirectionDepth" : 24.94 * mm});
        }
        {
            var Q0;
            {var subQ0=sQuery(id+"F23.wireOp",EDGE,"E69");var subQ1=sQuery(id+"F23.wireOp",EDGE,"E61");var subQ2=makeQuery(id+"F23.imprint","INTERSECT",VERTEX,{"derivedFrom":[subQ1,subQ0]});Q0=makeQuery(id+"F23.imprint","IMPRINT",FACE,{"disambiguationData":[TD([[makeQuery(id+"F23.imprint","IMPRINT",EDGE,{"disambiguationData":[TD([[subQ2,1.0]])],"derivedFrom":subQ1}),-1.0]])]});}
            var Q1;
            {var subQ0=sQuery(id+"F23.wireOp",EDGE,"E69");var subQ1=sQuery(id+"F23.wireOp",EDGE,"E59");var subQ2=makeQuery(id+"F23.imprint","INTERSECT",VERTEX,{"derivedFrom":[subQ1,subQ0]});Q1=makeQuery(id+"F23.imprint","IMPRINT",FACE,{"disambiguationData":[TD([[makeQuery(id+"F23.imprint","IMPRINT",EDGE,{"disambiguationData":[TD([[subQ2,1.0]])],"derivedFrom":subQ1}),-1.0]])]});}
            var Q2;
            {var subQ0=sQuery(id+"F23.wireOp",EDGE,"E69");var subQ1=sQuery(id+"F23.wireOp",EDGE,"E59");var subQ2=makeQuery(id+"F23.imprint","INTERSECT",VERTEX,{"derivedFrom":[subQ1,subQ0]});Q2=makeQuery(id+"F23.imprint","IMPRINT",FACE,{"disambiguationData":[TD([[makeQuery(id+"F23.imprint","IMPRINT",EDGE,{"disambiguationData":[TD([[subQ2,1.0]])],"derivedFrom":subQ1}),1.0]])]});}
            var Q3;
            {var subQ0=sQuery(id+"F23.wireOp",EDGE,"E69");var subQ1=sQuery(id+"F23.wireOp",EDGE,"E60");var subQ2=makeQuery(id+"F23.imprint","INTERSECT",VERTEX,{"derivedFrom":[subQ1,subQ0]});Q3=makeQuery(id+"F23.imprint","IMPRINT",FACE,{"disambiguationData":[TD([[makeQuery(id+"F23.imprint","IMPRINT",EDGE,{"disambiguationData":[TD([[subQ2,1.0]])],"derivedFrom":subQ1}),1.0]])]});}
            var Q4;
            {var subQ0=sQuery(id+"F23.wireOp",EDGE,"E69");var subQ1=sQuery(id+"F23.wireOp",EDGE,"E62");var subQ2=makeQuery(id+"F23.imprint","INTERSECT",VERTEX,{"derivedFrom":[subQ1,subQ0]});Q4=makeQuery(id+"F23.imprint","IMPRINT",FACE,{"disambiguationData":[TD([[makeQuery(id+"F23.imprint","IMPRINT",EDGE,{"disambiguationData":[TD([[subQ2,1.0]])],"derivedFrom":subQ1}),1.0]])]});}
            var Q5;
            {var subQ0=sQuery(id+"F23.wireOp",EDGE,"E69");var subQ1=sQuery(id+"F23.wireOp",EDGE,"E65");var subQ2=makeQuery(id+"F23.imprint","INTERSECT",VERTEX,{"derivedFrom":[subQ1,subQ0]});Q5=makeQuery(id+"F23.imprint","IMPRINT",FACE,{"disambiguationData":[TD([[makeQuery(id+"F23.imprint","IMPRINT",EDGE,{"disambiguationData":[TD([[subQ2,1.0]])],"derivedFrom":subQ1}),-1.0]])]});}
            var Q6;
            {var subQ0=sQuery(id+"F23.wireOp",EDGE,"E69");var subQ1=sQuery(id+"F23.wireOp",EDGE,"E66");var subQ2=makeQuery(id+"F23.imprint","INTERSECT",VERTEX,{"derivedFrom":[subQ1,subQ0]});Q6=makeQuery(id+"F23.imprint","IMPRINT",FACE,{"disambiguationData":[TD([[makeQuery(id+"F23.imprint","IMPRINT",EDGE,{"disambiguationData":[TD([[subQ2,1.0]])],"derivedFrom":subQ1}),1.0]])]});}
            extrude(context, id + "F29", {"entities" : qUnion([Q0, Q1, Q2, Q3, Q4, Q5, Q6]), "operationType" : NewBodyOperationType.ADD, "oppositeDirection" : true, "depth" : 47.9 * mm, "offsetDistance" : 25.4 * mm, "hasSecondDirection" : true, "secondDirectionOppositeDirection" : true, "secondDirectionDepth" : 46.63 * mm});
        }
        {
            var Q0;
            {var subQ0=sQuery(id+"F23.wireOp",EDGE,"E72");var subQ1=sQuery(id+"F23.wireOp",EDGE,"E65");var subQ2=makeQuery(id+"F23.imprint","INTERSECT",VERTEX,{"derivedFrom":[subQ1,subQ0]});Q0=makeQuery(id+"F23.imprint","IMPRINT",FACE,{"disambiguationData":[TD([[makeQuery(id+"F23.imprint","IMPRINT",EDGE,{"disambiguationData":[TD([[subQ2,-1.0]])],"derivedFrom":subQ1}),-1.0]])]});}
            var Q1;
            {var subQ0=sQuery(id+"F23.wireOp",EDGE,"E72");var subQ1=sQuery(id+"F23.wireOp",EDGE,"E61");var subQ2=makeQuery(id+"F23.imprint","INTERSECT",VERTEX,{"derivedFrom":[subQ1,subQ0]});Q1=makeQuery(id+"F23.imprint","IMPRINT",FACE,{"disambiguationData":[TD([[makeQuery(id+"F23.imprint","IMPRINT",EDGE,{"disambiguationData":[TD([[subQ2,-1.0]])],"derivedFrom":subQ1}),-1.0]])]});}
            var Q2;
            {var subQ0=sQuery(id+"F23.wireOp",EDGE,"E72");var subQ1=sQuery(id+"F23.wireOp",EDGE,"E59");var subQ2=makeQuery(id+"F23.imprint","INTERSECT",VERTEX,{"derivedFrom":[subQ1,subQ0]});Q2=makeQuery(id+"F23.imprint","IMPRINT",FACE,{"disambiguationData":[TD([[makeQuery(id+"F23.imprint","IMPRINT",EDGE,{"disambiguationData":[TD([[subQ2,-1.0]])],"derivedFrom":subQ1}),-1.0]])]});}
            var Q3;
            {var subQ0=sQuery(id+"F23.wireOp",EDGE,"E72");var subQ1=sQuery(id+"F23.wireOp",EDGE,"E59");var subQ2=makeQuery(id+"F23.imprint","INTERSECT",VERTEX,{"derivedFrom":[subQ1,subQ0]});Q3=makeQuery(id+"F23.imprint","IMPRINT",FACE,{"disambiguationData":[TD([[makeQuery(id+"F23.imprint","IMPRINT",EDGE,{"disambiguationData":[TD([[subQ2,-1.0]])],"derivedFrom":subQ1}),1.0]])]});}
            var Q4;
            {var subQ0=sQuery(id+"F23.wireOp",EDGE,"E72");var subQ1=sQuery(id+"F23.wireOp",EDGE,"E60");var subQ2=makeQuery(id+"F23.imprint","INTERSECT",VERTEX,{"derivedFrom":[subQ1,subQ0]});Q4=makeQuery(id+"F23.imprint","IMPRINT",FACE,{"disambiguationData":[TD([[makeQuery(id+"F23.imprint","IMPRINT",EDGE,{"disambiguationData":[TD([[subQ2,-1.0]])],"derivedFrom":subQ1}),1.0]])]});}
            var Q5;
            {var subQ0=sQuery(id+"F23.wireOp",EDGE,"E72");var subQ1=sQuery(id+"F23.wireOp",EDGE,"E62");var subQ2=makeQuery(id+"F23.imprint","INTERSECT",VERTEX,{"derivedFrom":[subQ1,subQ0]});Q5=makeQuery(id+"F23.imprint","IMPRINT",FACE,{"disambiguationData":[TD([[makeQuery(id+"F23.imprint","IMPRINT",EDGE,{"disambiguationData":[TD([[subQ2,-1.0]])],"derivedFrom":subQ1}),1.0]])]});}
            var Q6;
            {var subQ0=sQuery(id+"F23.wireOp",EDGE,"E72");var subQ1=sQuery(id+"F23.wireOp",EDGE,"E66");var subQ2=makeQuery(id+"F23.imprint","INTERSECT",VERTEX,{"derivedFrom":[subQ1,subQ0]});Q6=makeQuery(id+"F23.imprint","IMPRINT",FACE,{"disambiguationData":[TD([[makeQuery(id+"F23.imprint","IMPRINT",EDGE,{"disambiguationData":[TD([[subQ2,-1.0]])],"derivedFrom":subQ1}),1.0]])]});}
            extrude(context, id + "F30", {"entities" : qUnion([Q0, Q1, Q2, Q3, Q4, Q5, Q6]), "operationType" : NewBodyOperationType.ADD, "oppositeDirection" : true, "depth" : 47.9 * mm, "offsetDistance" : 25.4 * mm, "hasSecondDirection" : true, "secondDirectionOppositeDirection" : true, "secondDirectionDepth" : 42.53 * mm});
        }
    });
